# Revit family: Sanitary_Taps-Mixers_AXOR_51301CHN-AXOR-Waste-set-non-closing-for_new
name_source: partatom
category: Plumbing Fixtures
revit_build: Autodesk Revit 2018 (Build: 20170223_1515(x64)
units: mm (PartAtom-declared; Revit-internal decimal feet)

## family parameters
Cut with Voids When Loaded = Yes
Host = Face
OmniClass Number = 23.31.17.00
OmniClass Title = Showers
Part Type = Normal
Room Calculation Point = No
Round Connector Dimension = Use Diameter
Shared = No

## types (2) — shared parameters
Always visible = Yes
BIMobject category = Taps & Mixers
Connector Description = Water Outlet 31.8 mm
Default Elevation = 1219 mm
Description = AXOR Waste set non-closing for washbasins
Design country = Germany
Diameter = 32 mm
EAN code = 4059625361276
Edition number = 1
IFC Classification = Sanitary Terminal
Manufacturer = AXOR
Manufacturer country = Germany
Manufacturer name = AXOR
Masterformat 2014 Code = 22 41 23
Masterformat 2014 Description = Residential Showers
Model = 51301CHN
OmniClass Code = 23-31 17 00
OmniClass Description = Showers
Product Guid = 4fc7f350-8fe2-4d9b-98d3-8f457de9ab10
Product SKU = 51301CHN
Product data url = https://bimobject.com
Product family = AXOR
Product group = Waste set
Product name = AXOR Waste set non-closing for washbasins
Product url = https://www.axor-design.com
QR code = https://bimobject.com
UNSPSC Code = 301815
URL = https://www.axor-design.com
Uniclass 2015 Code = Pr_40_20_87_76
Uniclass 2015 Name = Shower heads
Uniformat II Code = D2010
Uniformat II Description = Plumbing Fixtures
Version = 1
Weight Net (Kg) = 195

## per-type parameters (varying)
| type | Material |
| 707 Matte White | AXOR - Metal - 707 Matte White |
| 677 Matte Black | AXOR - Metal - 677 Matte Black |

## geometry (parser evidence)
native form markers: Sweep x2
no freeform markers — native parametric forms only
